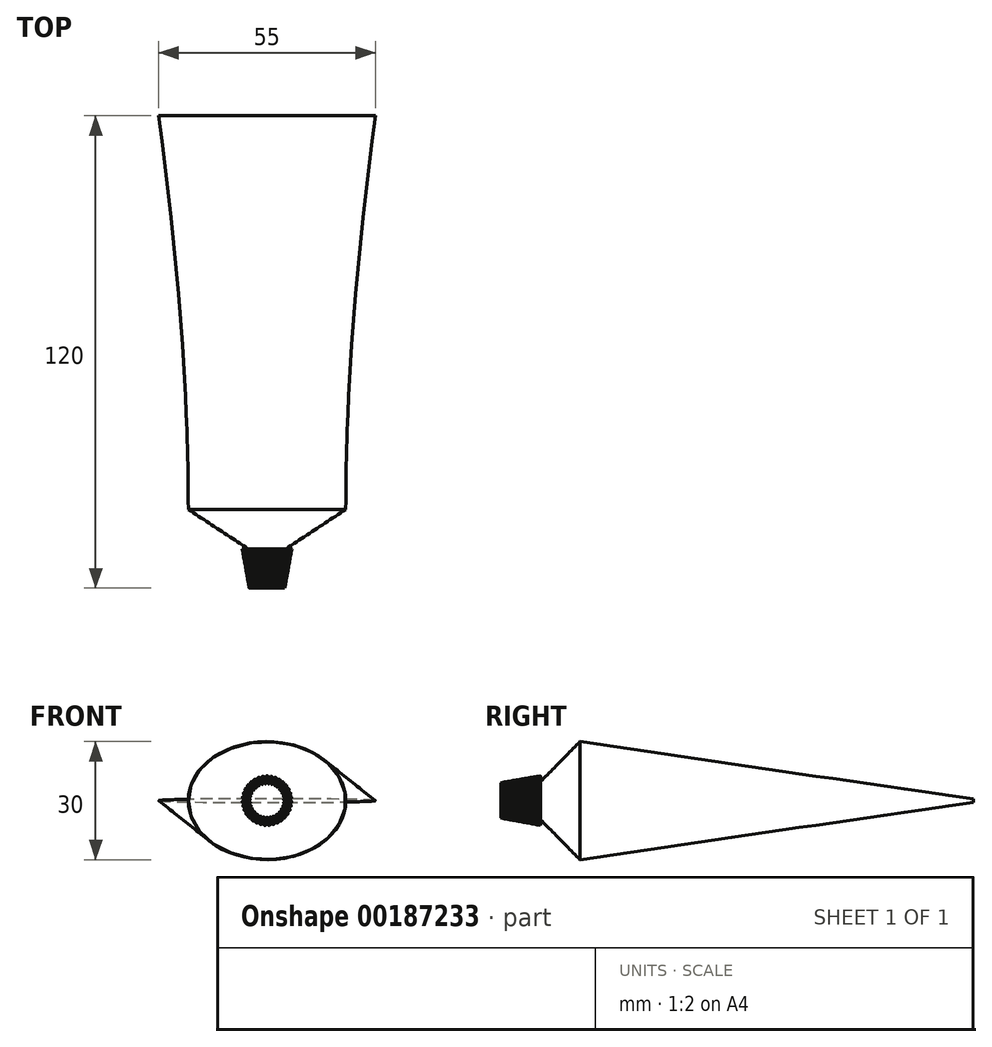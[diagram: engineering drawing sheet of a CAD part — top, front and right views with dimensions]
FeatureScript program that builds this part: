
annotation { "Feature Type Name" : "Feature", "Feature Type Description" : "" }
export const myFeature = defineFeature(function(context is Context, id is Id, definition is map)
    precondition{}
    {
        {
            var Q0;
            Q0=qCreatedBy(makeId("Front.planeOp"),FACE);
            cPlane(context, id + "F0", {"entities" : qUnion([Q0]), "cplaneType" : CPlaneType.OFFSET, "offset" : 100 * mm, "oppositeDirection" : true, "width" : 150 * mm, "height" : 150 * mm});
        }
        {
            var Q0;
            Q0=qCreatedBy(makeId("Front.planeOp"),FACE);
            var sketch = newSketch(context, id + "F1", { "sketchPlane" : qUnion([Q0])});
            skEllipse(sketch, "E0", {"center": v(0, 0) * mm, "majorRadius": 20 * mm, "minorRadius": 15 * mm, "majorAxis": v(-1, 0)});
            skSolve(sketch);
        }
        {
            var Q0;
            Q0=qCreatedBy(id+"F0.planeOp",FACE);
            var sketch = newSketch(context, id + "F2", { "sketchPlane" : qUnion([Q0])});
            skEllipse(sketch, "E1", {"center": v(0, 0) * mm, "majorRadius": 27.5 * mm, "minorRadius": 0.5 * mm, "majorAxis": v(-1, 0)});
            skSolve(sketch);
        }
        {
            var Q0;
            Q0 = qSketchRegion(id + "F1", true);
            var Q1;
            Q1 = qSketchRegion(id + "F2", true);
            loft(context, id + "F3", {"sheetProfilesArray" : [{ "sheetProfileEntities" : qUnion([Q0]) }, { "sheetProfileEntities" : qUnion([Q1]) }]});
        }
        {
            var Q0;
            Q0=makeQuery(id+"F1.imprint","IMPRINT",FACE,{"disambiguationData":[TD([[makeQuery(id+"F1.imprint","IMPRINT",EDGE,{"derivedFrom":sQuery(id+"F1.wireOp",EDGE,"E0")}),1.0]])]});
            cPlane(context, id + "F4", {"entities" : qUnion([Q0]), "cplaneType" : CPlaneType.OFFSET, "offset" : 10 * mm, "width" : 150 * mm, "height" : 150 * mm});
        }
        {
            var Q0;
            Q0=qCreatedBy(id+"F4.planeOp",FACE);
            var sketch = newSketch(context, id + "F5", { "sketchPlane" : qUnion([Q0])});
            skCircle(sketch, "E2", {"center": v(0, 0) * mm, "radius": 4.84 * mm});
            skSolve(sketch);
        }
        {
            var Q0;
            Q0=makeQuery(id+"F1.imprint","IMPRINT",FACE,{"disambiguationData":[TD([[makeQuery(id+"F1.imprint","IMPRINT",EDGE,{"derivedFrom":sQuery(id+"F1.wireOp",EDGE,"E0")}),1.0]])]});
            var Q1;
            Q1 = qSketchRegion(id + "F5", true);
            loft(context, id + "F6", {"sheetProfilesArray" : [{ "sheetProfileEntities" : qUnion([Q0]) }, { "sheetProfileEntities" : qUnion([Q1]) }]});
        }
        {
            var Q0;
            Q0=qCreatedBy(id+"F4.planeOp",FACE);
            var sketch = newSketch(context, id + "F7", { "sketchPlane" : qUnion([Q0])});
            skCircle(sketch, "E3", {"center": v(0, 0) * mm, "radius": 6 * mm});
            skSolve(sketch);
        }
        {
            var Q0;
            Q0 = qSketchRegion(id + "F7", true);
            extrude(context, id + "F8", {"entities" : qUnion([Q0]), "operationType" : NewBodyOperationType.ADD, "depth" : 10 * mm, "hasDraft" : true, "draftAngle" : 10 * degree, "draftPullDirection" : true});
        }
        {
            var Q0;
            Q0=qCreatedBy(id+"F4.planeOp",FACE);
            var sketch = newSketch(context, id + "F9", { "sketchPlane" : qUnion([Q0])});
            skCircle(sketch, "E4", {"center": v(0, 6) * mm, "radius": 0.3 * mm});
            skCircle(sketch, "E5.1.0", {"center": v(-1.07, 5.9) * mm, "radius": 0.3 * mm});
            skCircle(sketch, "E5.2.0", {"center": v(-2.1, 5.62) * mm, "radius": 0.3 * mm});
            skCircle(sketch, "E5.3.0", {"center": v(-3.08, 5.15) * mm, "radius": 0.3 * mm});
            skCircle(sketch, "E5.4.0", {"center": v(-3.95, 4.52) * mm, "radius": 0.3 * mm});
            skCircle(sketch, "E5.5.0", {"center": v(-4.7, 3.74) * mm, "radius": 0.3 * mm});
            skCircle(sketch, "E5.6.0", {"center": v(-5.28, 2.84) * mm, "radius": 0.3 * mm});
            skCircle(sketch, "E5.7.0", {"center": v(-5.7, 1.85) * mm, "radius": 0.3 * mm});
            skCircle(sketch, "E5.8.0", {"center": v(-5.95, 0.8) * mm, "radius": 0.3 * mm});
            skCircle(sketch, "E5.9.0", {"center": v(-6, -0.27) * mm, "radius": 0.3 * mm});
            skCircle(sketch, "E5.10.0", {"center": v(-5.85, -1.34) * mm, "radius": 0.3 * mm});
            skCircle(sketch, "E5.11.0", {"center": v(-5.52, -2.36) * mm, "radius": 0.3 * mm});
            skCircle(sketch, "E5.12.0", {"center": v(-5, -3.3) * mm, "radius": 0.3 * mm});
            skCircle(sketch, "E5.13.0", {"center": v(-4.34, -4.15) * mm, "radius": 0.3 * mm});
            skCircle(sketch, "E5.14.0", {"center": v(-3.53, -4.85) * mm, "radius": 0.3 * mm});
            skCircle(sketch, "E5.15.0", {"center": v(-2.6, -5.4) * mm, "radius": 0.3 * mm});
            skCircle(sketch, "E5.16.0", {"center": v(-1.6, -5.78) * mm, "radius": 0.3 * mm});
            skCircle(sketch, "E5.17.0", {"center": v(-0.54, -5.98) * mm, "radius": 0.3 * mm});
            skCircle(sketch, "E5.18.0", {"center": v(0.54, -5.98) * mm, "radius": 0.3 * mm});
            skCircle(sketch, "E5.19.0", {"center": v(1.6, -5.78) * mm, "radius": 0.3 * mm});
            skCircle(sketch, "E5.20.0", {"center": v(2.6, -5.4) * mm, "radius": 0.3 * mm});
            skCircle(sketch, "E5.21.0", {"center": v(3.53, -4.85) * mm, "radius": 0.3 * mm});
            skCircle(sketch, "E5.22.0", {"center": v(4.34, -4.15) * mm, "radius": 0.3 * mm});
            skCircle(sketch, "E5.23.0", {"center": v(5, -3.3) * mm, "radius": 0.3 * mm});
            skCircle(sketch, "E5.24.0", {"center": v(5.52, -2.36) * mm, "radius": 0.3 * mm});
            skCircle(sketch, "E5.25.0", {"center": v(5.85, -1.34) * mm, "radius": 0.3 * mm});
            skCircle(sketch, "E5.26.0", {"center": v(6, -0.27) * mm, "radius": 0.3 * mm});
            skCircle(sketch, "E5.27.0", {"center": v(5.95, 0.8) * mm, "radius": 0.3 * mm});
            skCircle(sketch, "E5.28.0", {"center": v(5.7, 1.85) * mm, "radius": 0.3 * mm});
            skCircle(sketch, "E5.29.0", {"center": v(5.28, 2.84) * mm, "radius": 0.3 * mm});
            skCircle(sketch, "E5.30.0", {"center": v(4.7, 3.74) * mm, "radius": 0.3 * mm});
            skCircle(sketch, "E5.31.0", {"center": v(3.95, 4.52) * mm, "radius": 0.3 * mm});
            skCircle(sketch, "E5.32.0", {"center": v(3.08, 5.15) * mm, "radius": 0.3 * mm});
            skCircle(sketch, "E5.33.0", {"center": v(2.1, 5.62) * mm, "radius": 0.3 * mm});
            skCircle(sketch, "E5.34.0", {"center": v(1.07, 5.9) * mm, "radius": 0.3 * mm});
            skPoint(sketch, "E5.center", {"position": v(0, 0) * mm});
            skCircle(sketch, "E6", {"center": v(0, 0) * mm, "radius": 6 * mm});
            skSolve(sketch);
        }
        {
            var Q0;
            Q0=makeQuery(id+"F8.opExtrude","CAP_FACE",FACE,{"disambiguationData":[OSD([sQuery(id+"F7.wireOp",EDGE,"E3")])],"isStart":false});
            var sketch = newSketch(context, id + "F10", { "sketchPlane" : qUnion([Q0])});
            skCircle(sketch, "E7", {"center": v(0, 4.26) * mm, "radius": 0.3 * mm});
            skCircle(sketch, "E8.1.0", {"center": v(-0.76, 4.2) * mm, "radius": 0.3 * mm});
            skCircle(sketch, "E8.2.0", {"center": v(-1.48, 4) * mm, "radius": 0.3 * mm});
            skCircle(sketch, "E8.3.0", {"center": v(-2.16, 3.67) * mm, "radius": 0.3 * mm});
            skCircle(sketch, "E8.4.0", {"center": v(-2.77, 3.23) * mm, "radius": 0.3 * mm});
            skCircle(sketch, "E8.5.0", {"center": v(-3.3, 2.68) * mm, "radius": 0.3 * mm});
            skCircle(sketch, "E8.6.0", {"center": v(-3.7, 2.05) * mm, "radius": 0.3 * mm});
            skCircle(sketch, "E8.7.0", {"center": v(-4, 1.36) * mm, "radius": 0.3 * mm});
            skCircle(sketch, "E8.8.0", {"center": v(-4.17, 0.63) * mm, "radius": 0.3 * mm});
            skCircle(sketch, "E8.9.0", {"center": v(-4.2, -0.13) * mm, "radius": 0.3 * mm});
            skCircle(sketch, "E8.10.0", {"center": v(-4.1, -0.87) * mm, "radius": 0.3 * mm});
            skCircle(sketch, "E8.11.0", {"center": v(-3.87, -1.59) * mm, "radius": 0.3 * mm});
            skCircle(sketch, "E8.12.0", {"center": v(-3.51, -2.25) * mm, "radius": 0.3 * mm});
            skCircle(sketch, "E8.13.0", {"center": v(-3.04, -2.84) * mm, "radius": 0.3 * mm});
            skCircle(sketch, "E8.14.0", {"center": v(-2.48, -3.33) * mm, "radius": 0.3 * mm});
            skCircle(sketch, "E8.15.0", {"center": v(-1.83, -3.72) * mm, "radius": 0.3 * mm});
            skCircle(sketch, "E8.16.0", {"center": v(-1.12, -3.99) * mm, "radius": 0.3 * mm});
            skCircle(sketch, "E8.17.0", {"center": v(-0.38, -4.12) * mm, "radius": 0.3 * mm});
            skCircle(sketch, "E8.18.0", {"center": v(0.37, -4.12) * mm, "radius": 0.3 * mm});
            skCircle(sketch, "E8.19.0", {"center": v(1.1, -3.99) * mm, "radius": 0.3 * mm});
            skCircle(sketch, "E8.20.0", {"center": v(1.81, -3.72) * mm, "radius": 0.3 * mm});
            skCircle(sketch, "E8.21.0", {"center": v(2.46, -3.33) * mm, "radius": 0.3 * mm});
            skCircle(sketch, "E8.22.0", {"center": v(3.03, -2.84) * mm, "radius": 0.3 * mm});
            skCircle(sketch, "E8.23.0", {"center": v(3.5, -2.25) * mm, "radius": 0.3 * mm});
            skCircle(sketch, "E8.24.0", {"center": v(3.85, -1.59) * mm, "radius": 0.3 * mm});
            skCircle(sketch, "E8.25.0", {"center": v(4.09, -0.87) * mm, "radius": 0.3 * mm});
            skCircle(sketch, "E8.26.0", {"center": v(4.19, -0.13) * mm, "radius": 0.3 * mm});
            skCircle(sketch, "E8.27.0", {"center": v(4.15, 0.63) * mm, "radius": 0.3 * mm});
            skCircle(sketch, "E8.28.0", {"center": v(3.99, 1.36) * mm, "radius": 0.3 * mm});
            skCircle(sketch, "E8.29.0", {"center": v(3.7, 2.05) * mm, "radius": 0.3 * mm});
            skCircle(sketch, "E8.30.0", {"center": v(3.28, 2.68) * mm, "radius": 0.3 * mm});
            skCircle(sketch, "E8.31.0", {"center": v(2.76, 3.23) * mm, "radius": 0.3 * mm});
            skCircle(sketch, "E8.32.0", {"center": v(2.15, 3.67) * mm, "radius": 0.3 * mm});
            skCircle(sketch, "E8.33.0", {"center": v(1.47, 4) * mm, "radius": 0.3 * mm});
            skCircle(sketch, "E8.34.0", {"center": v(0.74, 4.2) * mm, "radius": 0.3 * mm});
            skPoint(sketch, "E8.center", {"position": v(0, 0.06) * mm});
            skCircle(sketch, "E9", {"center": v(0, 0) * mm, "radius": 4.26 * mm});
            skSolve(sketch);
        }
        {
            var Q1;
            Q1 = qSketchRegion(id + "F9", true);
            var Q2;
            Q2 = qSketchRegion(id + "F10", true);
            loft(context, id + "F11", {"operationType" : NewBodyOperationType.ADD, "sheetProfilesArray" : [{ "sheetProfileEntities" : qUnion([Q1]) }, { "sheetProfileEntities" : qUnion([Q2]) }]});
        }
    });
